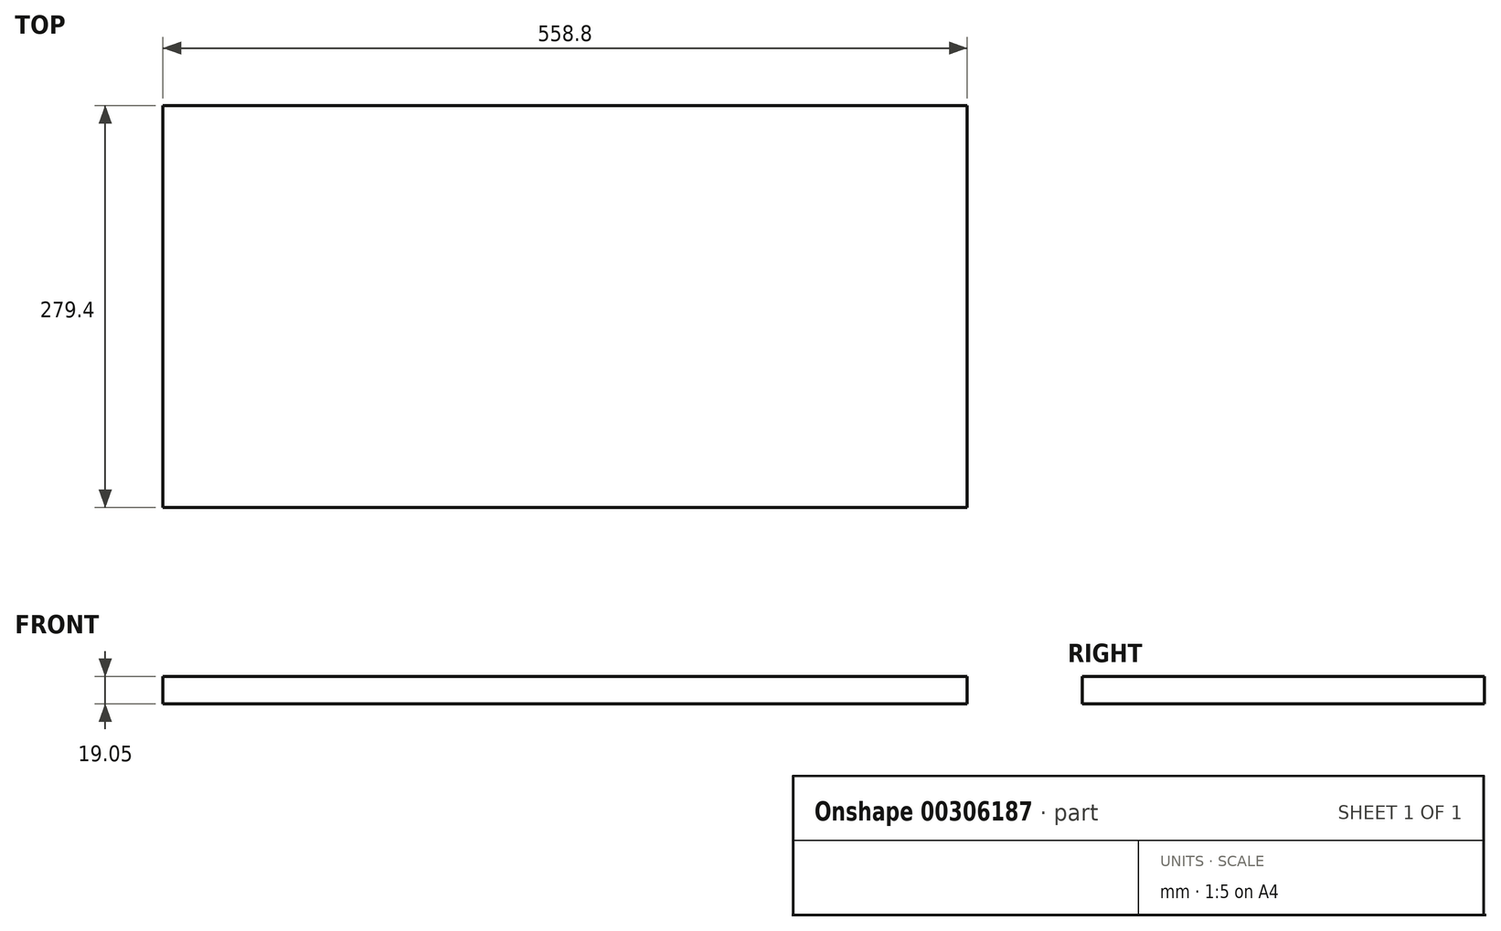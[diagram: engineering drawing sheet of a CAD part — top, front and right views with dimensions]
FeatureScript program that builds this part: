
annotation { "Feature Type Name" : "Feature", "Feature Type Description" : "" }
export const myFeature = defineFeature(function(context is Context, id is Id, definition is map)
    precondition{}
    {
        {
            var Q0;
            Q0=qCreatedBy(makeId("Top.planeOp"),FACE);
            var sketch = newSketch(context, id + "F0", { "sketchPlane" : qUnion([Q0])});
            skLineSegment(sketch, "E0.bottom", {"start": v(279.4, 139.7) * mm, "end": v(-279.4, 139.7) * mm});
            skLineSegment(sketch, "E0.top", {"start": v(279.4, -139.7) * mm, "end": v(-279.4, -139.7) * mm});
            skLineSegment(sketch, "E0.left", {"start": v(279.4, 139.7) * mm, "end": v(279.4, -139.7) * mm});
            skLineSegment(sketch, "E0.right", {"start": v(-279.4, 139.7) * mm, "end": v(-279.4, -139.7) * mm});
            skPoint(sketch, "E0.middle", {"position": v(0, 0) * mm});
            skSolve(sketch);
        }
        {
            var Q0;
            Q0=makeQuery(id+"F0.imprint","IMPRINT",FACE,{"disambiguationData":[TD([[makeQuery(id+"F0.imprint","IMPRINT",EDGE,{"derivedFrom":sQuery(id+"F0.wireOp",EDGE,"E0.bottom")}),1.0]])]});
            extrude(context, id + "F1", {"entities" : qUnion([Q0]), "depth" : 19.05 * mm});
        }
    });
